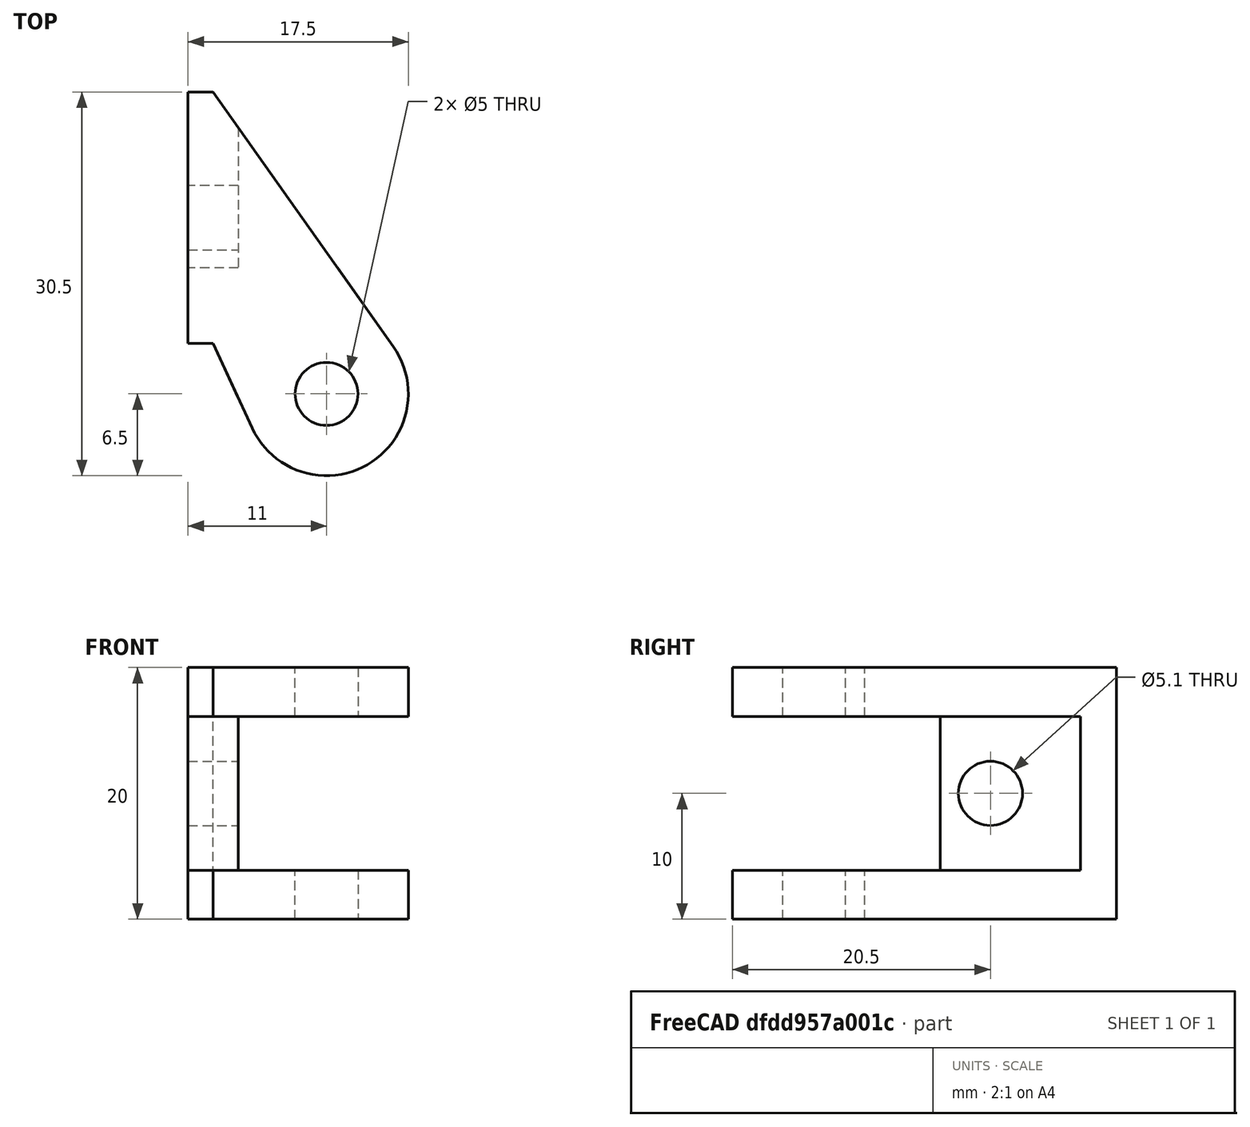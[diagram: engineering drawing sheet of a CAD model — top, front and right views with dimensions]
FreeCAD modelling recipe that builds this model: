
FCSTD DOCUMENT  (FreeCAD 0.19R23578 (Git))
Label: x_idler_bracket
License: All rights reserved
LicenseURL: http://en.wikipedia.org/wiki/All_rights_reserved
objects: TechDraw::DrawViewDimension×16, Sketcher::SketchObject×4, PartDesign::Pocket×3, TechDraw::DrawProjGroupItem×3, PartDesign::CoordinateSystem×2, PartDesign::Pad×1, PartDesign::Body×1, TechDraw::DrawSVGTemplate×1, App::Part×1, TechDraw::DrawViewPart×1, TechDraw::DrawProjGroup×1, TechDraw::DrawPage×1
note: 15 computed .brp shape members not serialized (recipe doc carries the construction recipe); baked Part::Feature solids carry a one-line shape summary decoded from their .brp

FEATURE [Sketcher::SketchObject] Sketch047
  MapMode = 5
  Support = -> [XY_Plane060]
  sketch-geometry (6):
    g0: ArcOfCircle CenterX=11 CenterY=-14 CenterZ=0 NormalX=0 NormalY=0 NormalZ=1 AngleXU=0 Radius=6.5 StartAngle=3.57338 EndAngle=6.89834
    g1: LineSegment StartX=0 StartY=-10 StartZ=0 EndX=0 EndY=10 EndZ=0
    g2: LineSegment StartX=0 StartY=10 StartZ=0 EndX=2 EndY=10 EndZ=0
    g3: LineSegment StartX=2 StartY=10 StartZ=0 EndX=16.3084 EndY=-10.2489 EndZ=0
    g4: LineSegment StartX=0 StartY=-10 StartZ=0 EndX=2 EndY=-10 EndZ=0
    g5: LineSegment StartX=2 StartY=-10 StartZ=0 EndX=5.09658 EndY=-16.7202 EndZ=0
  constraints (18):
    c: Vertical(g1)
    c: Coincident(g1,g2)
    c: Horizontal(g2)
    c: Coincident(g2,g3)
    c: Diameter(g0) = 13
    c: PointOnObject(g-1,g1)
    c: DistanceY(g-1,g1) = 10
    c: DistanceY(g1,g-1) = 10
    c: DistanceX(g2,g2) = 2
    c: DistanceX(g-1,g0) = 11
    c: DistanceY(g0,g-1) = 14
    c: Coincident(g1,g4)
    c: Coincident(g4,g5)
    c: Tangent(g5,g0)
    c: DistanceX(g4,g4) = 2
    c: Coincident(g5,g0)
    c: Horizontal(g4)
    c: Tangent(g3,g0) = 1.5708
FEATURE [PartDesign::Pad] Pad020  label="Pad021"
  AllowMultiFace = false
  Direction = (1,1,1)
  Length = 20
  Length2 = 100
  Midplane = true
  Profile = -> Sketch047
  Type = 0
FEATURE [Sketcher::SketchObject] Sketch048
  MapMode = 5
  Placement = pos=(0,0,0) rot=(0.57735,0.57735,0.57735;2.0944rad)
  Support = -> [YZ_Plane060]
  sketch-geometry (5):
    g0: LineSegment StartX=-24 StartY=6.1 StartZ=0 EndX=-4 EndY=6.1 EndZ=0
    g1: LineSegment StartX=-4 StartY=6.1 StartZ=0 EndX=-4 EndY=-6.1 EndZ=0
    g2: LineSegment StartX=-4 StartY=-6.1 StartZ=0 EndX=-24 EndY=-6.1 EndZ=0
    g3: LineSegment StartX=-24 StartY=-6.1 StartZ=0 EndX=-24 EndY=6.1 EndZ=0
    g4: Circle CenterX=0 CenterY=0 CenterZ=0 NormalX=0 NormalY=0 NormalZ=1 AngleXU=0 Radius=2.55
  constraints (12):
    c: Coincident(g0,g1)
    c: Coincident(g1,g2)
    c: Coincident(g2,g3)
    c: Coincident(g3,g0)
    c: Horizontal(g0)
    c: Symmetric(g2,g0,g-1)
    c: Symmetric(g0,g1,g-1)
    c: DistanceX(g0,g0) = 20
    c: DistanceY(g3,g3) = 12.2
    c: Coincident(g4,g-1)
    c: Diameter(g4) = 5.1
    c: DistanceX(g0,g4) = 4
FEATURE [Sketcher::SketchObject] Sketch049
  AttachmentOffset = pos=(0,0,4) rot=(0,0,1;0rad)
  MapMode = 5
  Placement = pos=(4,-9e-16,9e-16) rot=(0.57735,0.57735,0.57735;2.0944rad)
  Support = -> [YZ_Plane060]
  sketch-geometry (4):
    g0: LineSegment StartX=-25 StartY=6.1 StartZ=0 EndX=25 EndY=6.1 EndZ=0
    g1: LineSegment StartX=25 StartY=6.1 StartZ=0 EndX=25 EndY=-6.1 EndZ=0
    g2: LineSegment StartX=25 StartY=-6.1 StartZ=0 EndX=-25 EndY=-6.1 EndZ=0
    g3: LineSegment StartX=-25 StartY=-6.1 StartZ=0 EndX=-25 EndY=6.1 EndZ=0
  constraints (12):
    c: Coincident(g0,g1)
    c: Coincident(g1,g2)
    c: Coincident(g2,g3)
    c: Coincident(g3,g0)
    c: Horizontal(g0)
    c: Horizontal(g2)
    c: Vertical(g1)
    c: Vertical(g3)
    c: DistanceX(g0,g0) = 50
    c: DistanceX(g-1,g0) = 25
    c: DistanceY(g-1,g0) = 6.1
    c: DistanceY(g1,g1) = 12.2
FEATURE [PartDesign::Pocket] Pocket016
  AllowMultiFace = false
  BaseFeature = -> Pad020
  Length = 5
  Length2 = 100
  Midplane = true
  Profile = -> Sketch048
  Type = 1
FEATURE [PartDesign::Pocket] Pocket017
  AllowMultiFace = false
  BaseFeature = -> Pocket016
  Length = 5
  Length2 = 100
  Profile = -> Sketch049
  Reversed = true
  Type = 1
FEATURE [Sketcher::SketchObject] Sketch050
  MapMode = 5
  Support = -> [XY_Plane060]
  sketch-geometry (1):
    g0: Circle CenterX=11 CenterY=-14 CenterZ=0 NormalX=0 NormalY=0 NormalZ=1 AngleXU=0 Radius=2.5
  constraints (3):
    c: DistanceY(g0,g-1) = 14
    c: DistanceX(g-1,g0) = 11
    c: Diameter(g0) = 5
FEATURE [PartDesign::Pocket] Pocket018
  AllowMultiFace = false
  BaseFeature = -> Pocket017
  Length = 5
  Length2 = 100
  Midplane = true
  Profile = -> Sketch050
  Type = 1
FEATURE [PartDesign::Body] Body020
  Group = -> [Sketch047,Pad020,Sketch048,Sketch049,Pocket016,Pocket017,Sketch050,Pocket018]
  Origin = -> Origin060
  Tip = -> Pocket018
FEATURE [TechDraw::DrawSVGTemplate] Template004
  EditableTexts = Author=Alex Neufeld; DWG_num=2020-103; Date=15/05/2020; Revision=2; Scale=NTS; Subtitle=For use with 20T 2GT pulley; Title=X-Axis Idler Bracket
  Height = 215.9
  Orientation = 1
  Width = 279.4
FEATURE [PartDesign::CoordinateSystem] LCS_1
  AttacherType = Attacher::AttachEngine3D
  MapMode = 11
  Placement = pos=(0,0,2.776e-13) rot=(0.707107,0,0.707107;3.14159rad)
  Support = -> [Pocket018]
FEATURE [PartDesign::CoordinateSystem] LCS_2
  AttacherType = Attacher::AttachEngine3D
  MapMode = 45
  Placement = pos=(11,-14,0) rot=(0.57735,0.57735,0.57735;2.0944rad)
  Support = -> [Pocket018]
FEATURE [App::Part] Part033  label="x_idler_bracket"
  Group = -> [Body020,LCS_1,LCS_2]
  Origin = -> Origin051
FEATURE [TechDraw::DrawViewPart] View004
  CoarseView = false
  Direction = (0.577,-0.577,0.577)
  Focus = 100
  HardHidden = false
  IsoCount = 0
  IsoHidden = false
  IsoVisible = false
  LockPosition = true
  Perspective = false
  Rotation = 0
  ScaleType = 0
  SeamHidden = false
  SeamVisible = true
  SmoothHidden = false
  SmoothVisible = true
  Source = -> [Part033]
  X = 36.0346
  XDirection = (0.707,0.707,0)
  Y = 180.306
FEATURE [TechDraw::DrawProjGroupItem] ProjItem017  label="Front004"
  CoarseView = false
  Direction = (1,0,0)
  Focus = 100
  HardHidden = false
  IsoCount = 0
  IsoHidden = false
  IsoVisible = false
  LockPosition = true
  Perspective = false
  Rotation = 0
  RotationVector = (0,1,0)
  Scale = 2
  ScaleType = 2
  SeamHidden = false
  SeamVisible = true
  SmoothHidden = false
  SmoothVisible = true
  Source = -> [View004,Part033]
  Type = 0
  X = 0
  XDirection = (0,-1,1e-16)
  Y = 0
FEATURE [TechDraw::DrawProjGroupItem] ProjItem018  label="Bottom004"
  CoarseView = false
  Direction = (0,1e-16,1)
  Focus = 100
  HardHidden = false
  IsoCount = 0
  IsoHidden = false
  IsoVisible = false
  LockPosition = true
  Perspective = false
  Rotation = 0
  RotationVector = (1,0,0)
  Scale = 2
  ScaleType = 2
  SeamHidden = false
  SeamVisible = true
  SmoothHidden = false
  SmoothVisible = true
  Source = -> [View004,Part033]
  Type = 5
  X = 0
  XDirection = (0,-1,1e-16)
  Y = 64.4821
FEATURE [TechDraw::DrawProjGroupItem] ProjItem019  label="Left003"
  CoarseView = false
  Direction = (1e-16,1,-1e-16)
  Focus = 100
  HardHidden = false
  IsoCount = 0
  IsoHidden = false
  IsoVisible = false
  LockPosition = true
  Perspective = false
  Rotation = 0
  RotationVector = (1,0,0)
  Scale = 2
  ScaleType = 2
  SeamHidden = false
  SeamVisible = true
  SmoothHidden = false
  SmoothVisible = true
  Source = -> [View004,Part033]
  Type = 1
  X = 76
  XDirection = (1,-1e-16,0)
  Y = 0
FEATURE [TechDraw::DrawProjGroup] ProjGroup004
  Anchor = -> ProjItem017
  AutoDistribute = true
  LockPosition = false
  ProjectionType = 0
  Rotation = 0
  Scale = 2
  ScaleType = 2
  Source = -> [View004,Part033]
  Views = -> [ProjItem017,ProjItem018,ProjItem019]
  X = 118.879
  Y = 93.5714
  spacingX = 15
  spacingY = 15
FEATURE [TechDraw::DrawViewDimension] Dimension082
  Arbitrary = false
  ArbitraryTolerances = false
  FormatSpec = %.2f
  FormatSpecOverTolerance = %+.2f
  FormatSpecUnderTolerance = %+.2f
  Inverted = false
  LockPosition = false
  MeasureType = 1
  OverTolerance = 0
  References2D = -> [ProjItem018]
  Rotation = 0
  ScaleType = 0
  TheoreticalExact = false
  Type = 2
  UnderTolerance = 0
  X = -38.4355
  Y = -15.5
FEATURE [TechDraw::DrawViewDimension] Dimension083
  Arbitrary = false
  ArbitraryTolerances = false
  FormatSpec = %.2f
  FormatSpecOverTolerance = %+.2f
  FormatSpecUnderTolerance = %+.2f
  Inverted = false
  LockPosition = false
  MeasureType = 1
  OverTolerance = 0
  References2D = -> [ProjItem018]
  Rotation = 0
  ScaleType = 0
  TheoreticalExact = false
  Type = 2
  UnderTolerance = 0
  X = 37.4428
  Y = -7.00652
FEATURE [TechDraw::DrawViewDimension] Dimension084
  Arbitrary = false
  ArbitraryTolerances = false
  FormatSpec = %.2f
  FormatSpecOverTolerance = %+.2f
  FormatSpecUnderTolerance = %+.2f
  Inverted = false
  LockPosition = false
  MeasureType = 1
  OverTolerance = 0
  References2D = -> [ProjItem018]
  Rotation = 0
  ScaleType = 0
  TheoreticalExact = false
  Type = 1
  UnderTolerance = 0
  X = -8.18841
  Y = 28.9239
FEATURE [TechDraw::DrawViewDimension] Dimension085
  Arbitrary = false
  ArbitraryTolerances = false
  FormatSpec = R%.2f
  FormatSpecOverTolerance = %+.2f
  FormatSpecUnderTolerance = %+.2f
  Inverted = false
  LockPosition = false
  MeasureType = 1
  OverTolerance = 0
  References2D = -> [ProjItem018]
  Rotation = 0
  ScaleType = 0
  TheoreticalExact = false
  Type = 4
  UnderTolerance = 0
  X = 38.8334
  Y = 18.066
FEATURE [TechDraw::DrawViewDimension] Dimension086
  Arbitrary = false
  ArbitraryTolerances = false
  FormatSpec = ⌀%.2f
  FormatSpecOverTolerance = %+.2f
  FormatSpecUnderTolerance = %+.2f
  Inverted = false
  LockPosition = false
  MeasureType = 1
  OverTolerance = 0
  References2D = -> [ProjItem018]
  Rotation = 0
  ScaleType = 0
  TheoreticalExact = false
  Type = 5
  UnderTolerance = 0
  X = 6.07827
  Y = -4.13322
FEATURE [TechDraw::DrawViewDimension] Dimension087
  Arbitrary = false
  ArbitraryTolerances = false
  FormatSpec = %.2f
  FormatSpecOverTolerance = %+.2f
  FormatSpecUnderTolerance = %+.2f
  Inverted = false
  LockPosition = false
  MeasureType = 1
  OverTolerance = 0
  References2D = -> [ProjItem018]
  Rotation = 0
  ScaleType = 0
  TheoreticalExact = false
  Type = 1
  UnderTolerance = 0
  X = -10.1623
  Y = -23.4094
FEATURE [TechDraw::DrawViewDimension] Dimension088
  Arbitrary = false
  ArbitraryTolerances = false
  FormatSpec = %.2f
  FormatSpecOverTolerance = %+.2f
  FormatSpecUnderTolerance = %+.2f
  Inverted = false
  LockPosition = false
  MeasureType = 1
  OverTolerance = 0
  References2D = -> [ProjItem018]
  Rotation = 0
  ScaleType = 0
  TheoreticalExact = false
  Type = 6
  UnderTolerance = 0
  X = -8.44204
  Y = -7.93551
FEATURE [TechDraw::DrawViewDimension] Dimension089
  Arbitrary = false
  ArbitraryTolerances = false
  FormatSpec = %.2f
  FormatSpecOverTolerance = %+.2f
  FormatSpecUnderTolerance = %+.2f
  Inverted = false
  LockPosition = false
  MeasureType = 1
  OverTolerance = 0
  References2D = -> [ProjItem017]
  Rotation = 0
  ScaleType = 0
  TheoreticalExact = false
  Type = 1
  UnderTolerance = 0
  X = -20.2974
  Y = 25.9805
FEATURE [TechDraw::DrawViewDimension] Dimension090
  Arbitrary = false
  ArbitraryTolerances = false
  FormatSpec = %.2f
  FormatSpecOverTolerance = %+.2f
  FormatSpecUnderTolerance = %+.2f
  Inverted = false
  LockPosition = false
  MeasureType = 1
  OverTolerance = 0
  References2D = -> [ProjItem017]
  Rotation = 0
  ScaleType = 0
  TheoreticalExact = false
  Type = 2
  UnderTolerance = 0
  X = -45.5396
  Y = -8.78435
FEATURE [TechDraw::DrawViewDimension] Dimension091
  Arbitrary = false
  ArbitraryTolerances = false
  FormatSpec = %.2f
  FormatSpecOverTolerance = %+.2f
  FormatSpecUnderTolerance = %+.2f
  Inverted = false
  LockPosition = false
  MeasureType = 1
  OverTolerance = 0
  References2D = -> [ProjItem017]
  Rotation = 0
  ScaleType = 0
  TheoreticalExact = false
  Type = 1
  UnderTolerance = 0
  X = 1.01304
  Y = -29.1174
FEATURE [TechDraw::DrawViewDimension] Dimension092
  Arbitrary = false
  ArbitraryTolerances = false
  FormatSpec = %.2f
  FormatSpecOverTolerance = %+.2f
  FormatSpecUnderTolerance = %+.2f
  Inverted = false
  LockPosition = false
  MeasureType = 1
  OverTolerance = 0
  References2D = -> [ProjItem017]
  Rotation = 0
  ScaleType = 0
  TheoreticalExact = false
  Type = 2
  UnderTolerance = 0
  X = -52.8948
  Y = -0.11725
FEATURE [TechDraw::DrawViewDimension] Dimension093
  Arbitrary = false
  ArbitraryTolerances = false
  FormatSpec = %.2f
  FormatSpecOverTolerance = %+.2f
  FormatSpecUnderTolerance = %+.2f
  Inverted = false
  LockPosition = false
  MeasureType = 1
  OverTolerance = 0
  References2D = -> [ProjItem019]
  Rotation = 0
  ScaleType = 0
  TheoreticalExact = false
  Type = 1
  UnderTolerance = 0
  X = -0.330424
  Y = -36.192
FEATURE [TechDraw::DrawViewDimension] Dimension094
  Arbitrary = false
  ArbitraryTolerances = false
  FormatSpec = %.2f
  FormatSpecOverTolerance = %+.2f
  FormatSpecUnderTolerance = %+.2f
  Inverted = false
  LockPosition = false
  MeasureType = 1
  OverTolerance = 0
  References2D = -> [ProjItem019]
  Rotation = 0
  ScaleType = 0
  TheoreticalExact = false
  Type = 1
  UnderTolerance = 0
  X = -1.85725
  Y = 28.1044
FEATURE [TechDraw::DrawViewDimension] Dimension095
  Arbitrary = false
  ArbitraryTolerances = false
  FormatSpec = %.2f
  FormatSpecOverTolerance = %+.2f
  FormatSpecUnderTolerance = %+.2f
  Inverted = false
  LockPosition = false
  MeasureType = 1
  OverTolerance = 0
  References2D = -> [ProjItem019]
  Rotation = 0
  ScaleType = 0
  TheoreticalExact = false
  Type = 2
  UnderTolerance = 0
  X = 23.4094
  Y = 0.506522
FEATURE [TechDraw::DrawViewDimension] Dimension096
  Arbitrary = false
  ArbitraryTolerances = false
  FormatSpec = %.2f
  FormatSpecOverTolerance = %+.2f
  FormatSpecUnderTolerance = %+.2f
  Inverted = false
  LockPosition = false
  MeasureType = 1
  OverTolerance = 0
  References2D = -> [ProjItem017]
  Rotation = 0
  ScaleType = 0
  TheoreticalExact = false
  Type = 1
  UnderTolerance = 0
  X = 13.6623
  Y = -1.05651
FEATURE [TechDraw::DrawViewDimension] Dimension097
  Arbitrary = false
  ArbitraryTolerances = false
  FormatSpec = ⌀%.2f
  FormatSpecOverTolerance = %+.2f
  FormatSpecUnderTolerance = %+.2f
  Inverted = false
  LockPosition = false
  MeasureType = 1
  OverTolerance = 0
  References2D = -> [ProjItem017]
  Rotation = 0
  ScaleType = 0
  TheoreticalExact = false
  Type = 5
  UnderTolerance = 0
  X = 4.37635
  Y = 6.07827
FEATURE [TechDraw::DrawPage] Page004  label="x_idler_bracket_dwg001"
  KeepUpdated = false
  NextBalloonIndex = 1
  ProjectionType = 0
  Template = -> Template004
  Views = -> [View004,ProjGroup004,Dimension082,Dimension083,Dimension084,Dimension085,Dimension086,Dimension087,Dimension088,Dimension089,Dimension090,Dimension091,Dimension092,Dimension093,Dimension094,Dimension095,Dimension096,Dimension097]
